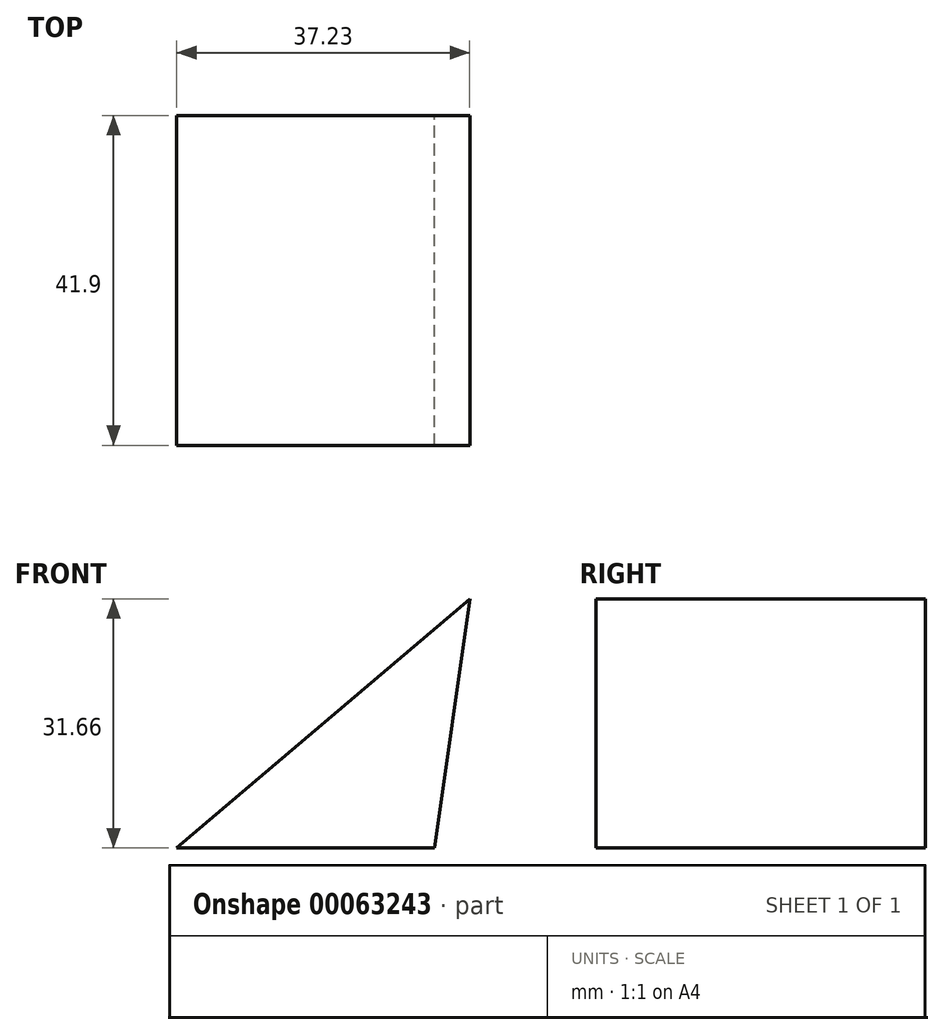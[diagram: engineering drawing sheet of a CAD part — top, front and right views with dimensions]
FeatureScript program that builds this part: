
annotation { "Feature Type Name" : "Feature", "Feature Type Description" : "" }
export const myFeature = defineFeature(function(context is Context, id is Id, definition is map)
    precondition{}
    {
        {
            var Q0;
            Q0=qCreatedBy(makeId("Front.planeOp"),FACE);
            var sketch = newSketch(context, id + "F0", { "sketchPlane" : qUnion([Q0])});
            skLineSegment(sketch, "E0", {"start": v(0, 0) * mm, "end": v(37.23, 31.66) * mm});
            skLineSegment(sketch, "E1", {"start": v(0, 0) * mm, "end": v(32.77, 0) * mm});
            skLineSegment(sketch, "E2", {"start": v(37.23, 31.66) * mm, "end": v(32.77, 0) * mm});
            skSolve(sketch);
        }
        {
            var Q0;
            Q0=makeQuery(id+"F0.imprint","IMPRINT",FACE,{"disambiguationData":[TD([[makeQuery(id+"F0.imprint","IMPRINT",EDGE,{"derivedFrom":sQuery(id+"F0.wireOp",EDGE,"E0")}),-1.0]])]});
            extrude(context, id + "F1", {"entities" : qUnion([Q0]), "depth" : 41.9 * mm});
        }
    });
